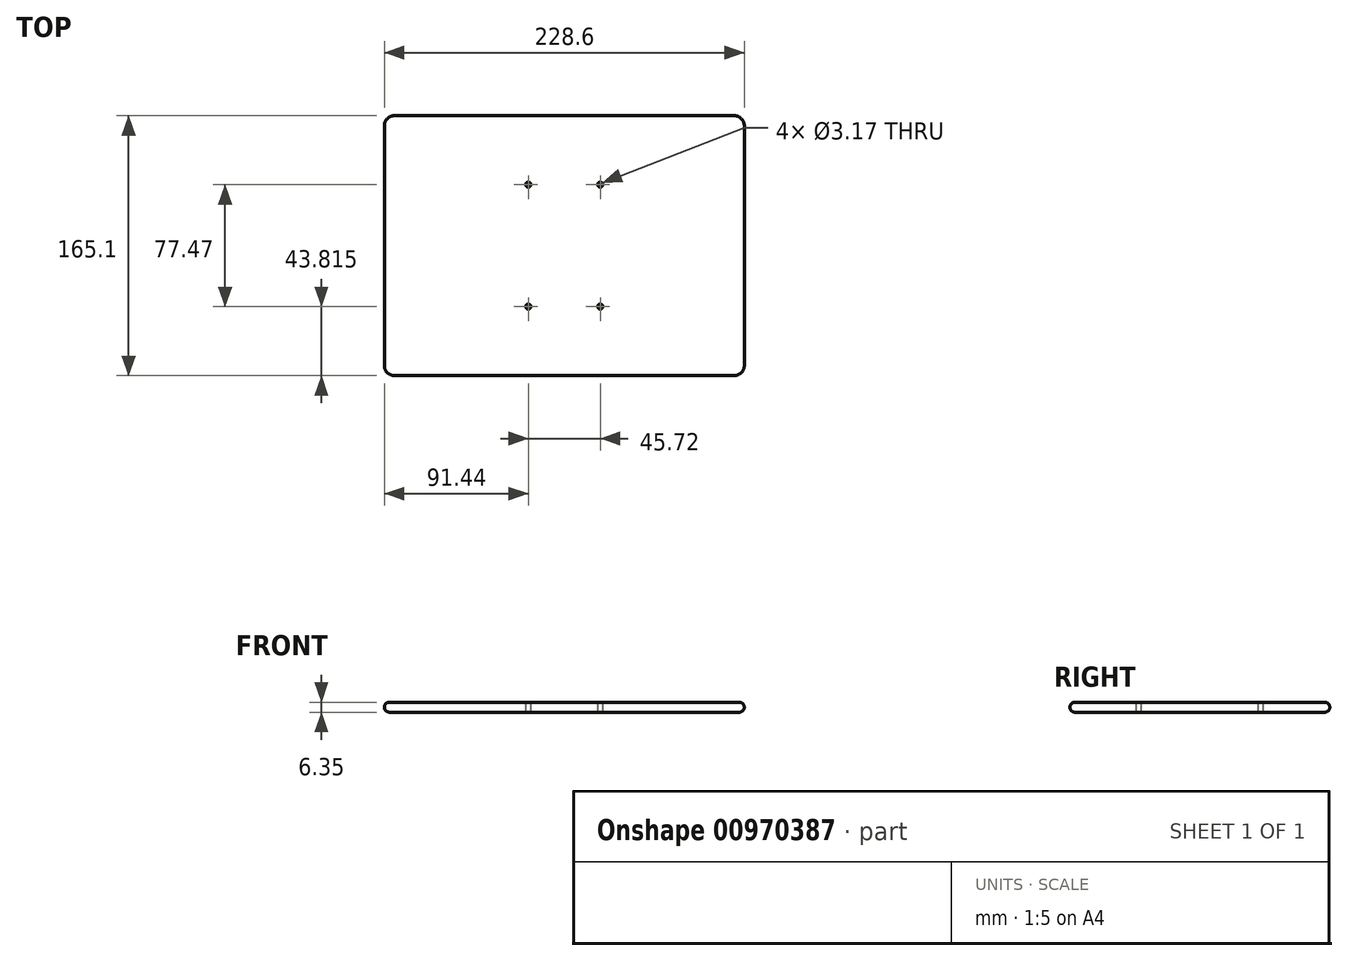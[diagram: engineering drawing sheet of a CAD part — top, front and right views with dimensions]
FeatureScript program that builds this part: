
annotation { "Feature Type Name" : "Feature", "Feature Type Description" : "" }
export const myFeature = defineFeature(function(context is Context, id is Id, definition is map)
    precondition{}
    {
        {
            var Q0;
            Q0=qCreatedBy(makeId("Top.planeOp"),FACE);
            var sketch = newSketch(context, id + "F0", { "sketchPlane" : qUnion([Q0])});
            skLineSegment(sketch, "E0.bottom", {"start": v(107.95, 82.55) * mm, "end": v(-107.95, 82.55) * mm});
            skLineSegment(sketch, "E0.top", {"start": v(107.95, -82.55) * mm, "end": v(-107.95, -82.55) * mm});
            skLineSegment(sketch, "E0.left", {"start": v(114.3, 76.2) * mm, "end": v(114.3, -76.2) * mm});
            skLineSegment(sketch, "E0.right", {"start": v(-114.3, 76.2) * mm, "end": v(-114.3, -76.2) * mm});
            skPoint(sketch, "E0.middle", {"position": v(0, 0) * mm});
            skPoint(sketch, "E1.visualSharp", {"position": v(-114.3, 82.55) * mm});
            skArc(sketch, "E1.filletArc", {"start": v(-107.95, 82.55) * mm, "mid": v(-112.44, 80.7) * mm, "end": v(-114.3, 76.2) * mm});
            skPoint(sketch, "E2.visualSharp", {"position": v(114.3, 82.55) * mm});
            skArc(sketch, "E2.filletArc", {"start": v(114.3, 76.2) * mm, "mid": v(112.44, 80.7) * mm, "end": v(107.95, 82.55) * mm});
            skPoint(sketch, "E3.visualSharp", {"position": v(114.3, -82.55) * mm});
            skArc(sketch, "E3.filletArc", {"start": v(107.95, -82.55) * mm, "mid": v(112.44, -80.7) * mm, "end": v(114.3, -76.2) * mm});
            skPoint(sketch, "E4.visualSharp", {"position": v(-114.3, -82.55) * mm});
            skArc(sketch, "E4.filletArc", {"start": v(-114.3, -76.2) * mm, "mid": v(-112.44, -80.7) * mm, "end": v(-107.95, -82.55) * mm});
            skSolve(sketch);
        }
        {
            var Q0;
            Q0 = qSketchRegion(id + "F0", true);
            extrude(context, id + "F1", {"entities" : qUnion([Q0]), "depth" : 6.35 * mm, "offsetDistance" : 25.4 * mm});
        }
        {
            var Q0;
            Q0=makeQuery(id+"F1.opExtrude","CAP_FACE",FACE,{"disambiguationData":[OSD([sQuery(id+"F0.wireOp",EDGE,"E0.bottom"),sQuery(id+"F0.wireOp",EDGE,"E0.top"),sQuery(id+"F0.wireOp",EDGE,"E0.left"),sQuery(id+"F0.wireOp",EDGE,"E0.right"),sQuery(id+"F0.wireOp",EDGE,"E1.filletArc"),sQuery(id+"F0.wireOp",EDGE,"E2.filletArc"),sQuery(id+"F0.wireOp",EDGE,"E3.filletArc"),sQuery(id+"F0.wireOp",EDGE,"E4.filletArc")])],"isStart":false});
            var Q1;
            Q1=makeQuery(id+"F1.opExtrude","CAP_FACE",FACE,{"disambiguationData":[OSD([sQuery(id+"F0.wireOp",EDGE,"E0.bottom"),sQuery(id+"F0.wireOp",EDGE,"E0.top"),sQuery(id+"F0.wireOp",EDGE,"E0.left"),sQuery(id+"F0.wireOp",EDGE,"E0.right"),sQuery(id+"F0.wireOp",EDGE,"E1.filletArc"),sQuery(id+"F0.wireOp",EDGE,"E2.filletArc"),sQuery(id+"F0.wireOp",EDGE,"E3.filletArc"),sQuery(id+"F0.wireOp",EDGE,"E4.filletArc")])],"isStart":true});
            fillet(context, id + "F2", {"entities" : qUnion([Q0, Q1]), "radius" : 3.17 * mm, "tangentPropagation" : true, "allowEdgeOverflow" : false});
        }
        {
            var Q0;
            Q0=makeQuery(id+"F1.opExtrude","CAP_FACE",FACE,{"disambiguationData":[OSD([sQuery(id+"F0.wireOp",EDGE,"E0.bottom"),sQuery(id+"F0.wireOp",EDGE,"E0.top"),sQuery(id+"F0.wireOp",EDGE,"E0.left"),sQuery(id+"F0.wireOp",EDGE,"E0.right"),sQuery(id+"F0.wireOp",EDGE,"E1.filletArc"),sQuery(id+"F0.wireOp",EDGE,"E2.filletArc"),sQuery(id+"F0.wireOp",EDGE,"E3.filletArc"),sQuery(id+"F0.wireOp",EDGE,"E4.filletArc")])],"isStart":false});
            var sketch = newSketch(context, id + "F3", { "sketchPlane" : qUnion([Q0])});
            skLineSegment(sketch, "E5", {"start": v(-111.13, 0) * mm, "end": v(0, 0) * mm, "construction": true});
            skLineSegment(sketch, "E6", {"start": v(0, 79.38) * mm, "end": v(0, 0) * mm, "construction": true});
            skPoint(sketch, "E7.orphan", {"position": v(0, -79.38) * mm});
            skPoint(sketch, "E8.orphan", {"position": v(111.13, 0) * mm});
            skCircle(sketch, "E9", {"center": v(-22.86, 38.73) * mm, "radius": 1.59 * mm});
            skCircle(sketch, "E10.MirrorC", {"center": v(22.86, 38.74) * mm, "radius": 1.59 * mm});
            skCircle(sketch, "E11.MirrorC", {"center": v(-22.86, -38.74) * mm, "radius": 1.59 * mm});
            skCircle(sketch, "E12.MirrorC", {"center": v(22.86, -38.74) * mm, "radius": 1.59 * mm});
            skSolve(sketch);
        }
        {
            var Q0;
            Q0 = qSketchRegion(id + "F3", true);
            extrude(context, id + "F4", {"entities" : qUnion([Q0]), "operationType" : NewBodyOperationType.REMOVE, "endBound" : BoundingType.THROUGH_ALL, "oppositeDirection" : true, "depth" : 25.4 * mm, "offsetDistance" : 25.4 * mm});
        }
    });
